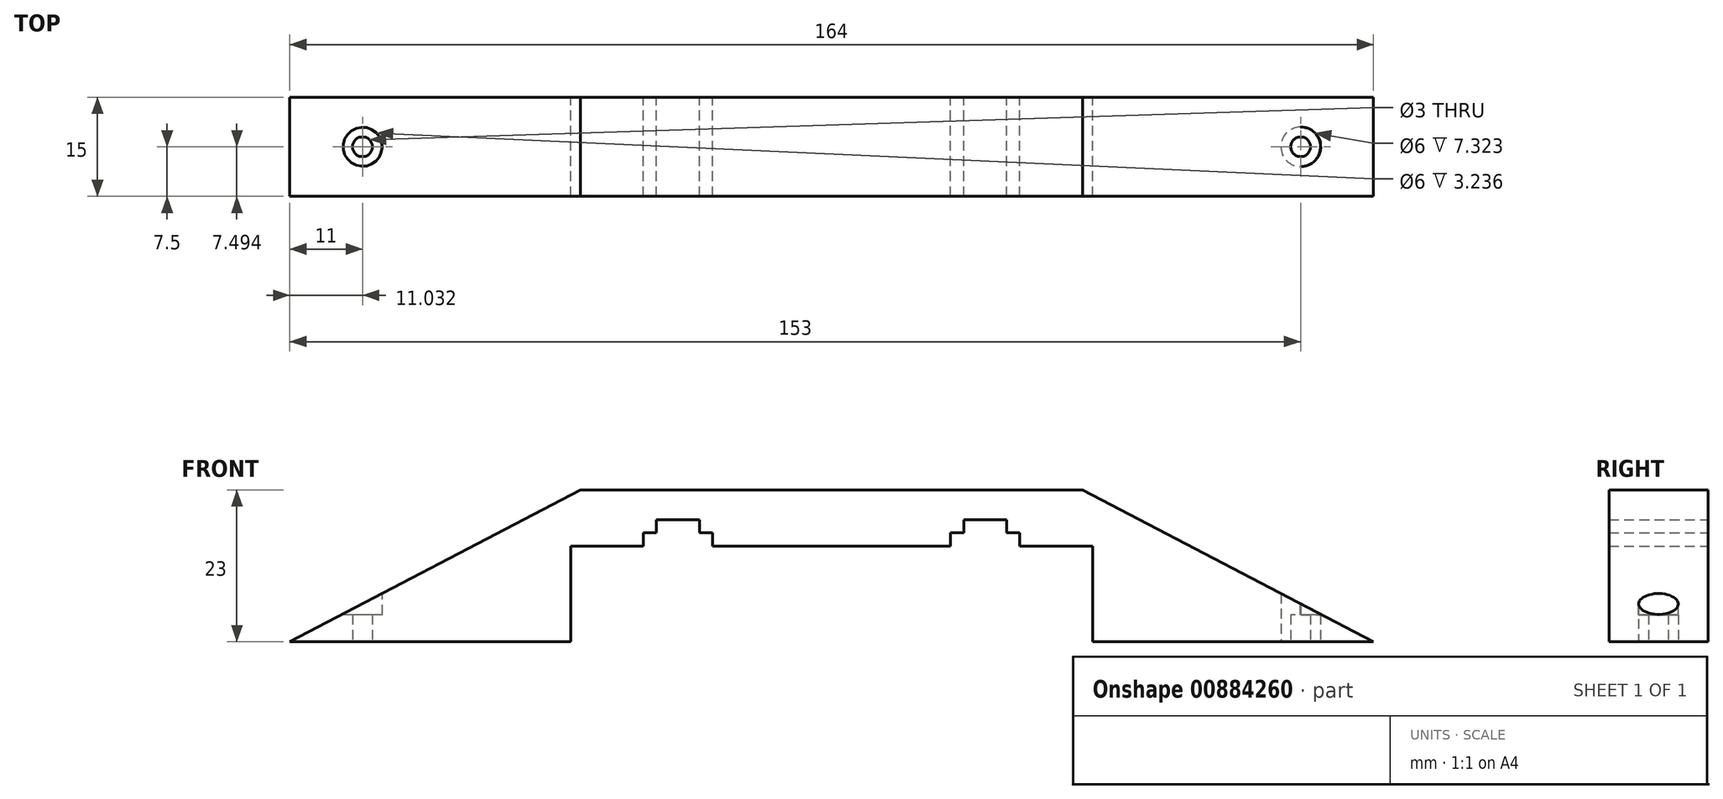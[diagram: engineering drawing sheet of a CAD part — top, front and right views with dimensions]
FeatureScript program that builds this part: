
annotation { "Feature Type Name" : "Feature", "Feature Type Description" : "" }
export const myFeature = defineFeature(function(context is Context, id is Id, definition is map)
    precondition{}
    {
        {
            var Q0;
            Q0=qCreatedBy(makeId("Top.planeOp"),FACE);
            cPlane(context, id + "F0", {"entities" : qUnion([Q0]), "cplaneType" : CPlaneType.OFFSET, "offset" : 8.6 * mm, "width" : 150 * mm, "height" : 150 * mm});
        }
        {
            var Q0;
            Q0=qCreatedBy(makeId("Front.planeOp"),FACE);
            var sketch = newSketch(context, id + "F1", { "sketchPlane" : qUnion([Q0])});
            skLineSegment(sketch, "E0", {"start": v(0, 122.54) * mm, "end": v(0, -122.54) * mm, "construction": true});
            skLineSegment(sketch, "E1", {"start": v(-39.5, 0) * mm, "end": v(-82, 0) * mm});
            skLineSegment(sketch, "E2", {"start": v(0, 0) * mm, "end": v(0, 14.5) * mm});
            skLineSegment(sketch, "E3", {"start": v(0, 23) * mm, "end": v(-38, 23) * mm});
            skLineSegment(sketch, "E4", {"start": v(-38, 23) * mm, "end": v(-82, 0) * mm});
            skLineSegment(sketch, "E5.top", {"start": v(0, 14.5) * mm, "end": v(-18, 14.5) * mm});
            skLineSegment(sketch, "E5.right", {"start": v(-39.5, 0) * mm, "end": v(-39.5, 14.5) * mm});
            skLineSegment(sketch, "E6.0", {"start": v(-20, 122.54) * mm, "end": v(-20, 16.5) * mm, "construction": true});
            skLineSegment(sketch, "E7.top", {"start": v(-20, 18.5) * mm, "end": v(-26.5, 18.5) * mm});
            skLineSegment(sketch, "E7.left", {"start": v(-20, 14.5) * mm, "end": v(-20, 18.5) * mm});
            skLineSegment(sketch, "E7.right", {"start": v(-26.5, 16.5) * mm, "end": v(-26.5, 18.5) * mm});
            skLineSegment(sketch, "E8.trimOffspring", {"start": v(-28.5, 14.5) * mm, "end": v(-39.5, 14.5) * mm});
            skLineSegment(sketch, "E9.MirrorCS", {"start": v(0, 23) * mm, "end": v(38, 23) * mm});
            skLineSegment(sketch, "E10.MirrorCS", {"start": v(38, 23) * mm, "end": v(82, 0) * mm});
            skLineSegment(sketch, "E11.MirrorCS", {"start": v(39.5, 0) * mm, "end": v(82, 0) * mm});
            skLineSegment(sketch, "E12.MirrorCS", {"start": v(39.5, 0) * mm, "end": v(39.5, 14.5) * mm});
            skLineSegment(sketch, "E13.MirrorCS", {"start": v(28.5, 14.5) * mm, "end": v(39.5, 14.5) * mm});
            skLineSegment(sketch, "E14.MirrorCS", {"start": v(20, 18.5) * mm, "end": v(26.5, 18.5) * mm});
            skLineSegment(sketch, "E15.MirrorCS", {"start": v(0, 14.5) * mm, "end": v(18, 14.5) * mm});
            skLineSegment(sketch, "E16.MirrorCS", {"start": v(20, 16.5) * mm, "end": v(20, 18.5) * mm});
            skLineSegment(sketch, "E17.MirrorCS", {"start": v(26.5, 16.5) * mm, "end": v(26.5, 18.5) * mm});
            skPoint(sketch, "E18.oppositeSnap0", {"position": v(-20, 16.5) * mm});
            skLineSegment(sketch, "E18.top", {"start": v(-28.5, 16.5) * mm, "end": v(-26.5, 16.5) * mm});
            skLineSegment(sketch, "E18.left", {"start": v(-28.5, 14.5) * mm, "end": v(-28.5, 16.5) * mm});
            skLineSegment(sketch, "E18.right", {"start": v(-18, 14.5) * mm, "end": v(-18, 16.5) * mm});
            skLineSegment(sketch, "E19.trimOffspring", {"start": v(-20, 16.5) * mm, "end": v(-18, 16.5) * mm});
            skPoint(sketch, "E20.orphan", {"position": v(-26.5, 14.5) * mm});
            skLineSegment(sketch, "E21.trimOffspring", {"start": v(-20, 14.5) * mm, "end": v(-20, -122.54) * mm, "construction": true});
            skLineSegment(sketch, "E22.MirrorCS", {"start": v(28.5, 16.5) * mm, "end": v(26.5, 16.5) * mm});
            skLineSegment(sketch, "E23.MirrorCS", {"start": v(28.5, 14.5) * mm, "end": v(28.5, 16.5) * mm});
            skLineSegment(sketch, "E24.MirrorCS", {"start": v(20, 16.5) * mm, "end": v(18, 16.5) * mm});
            skLineSegment(sketch, "E25.MirrorCS", {"start": v(18, 14.5) * mm, "end": v(18, 16.5) * mm});
            skPoint(sketch, "E26.orphan", {"position": v(20, 14.5) * mm});
            skPoint(sketch, "E27.orphan", {"position": v(26.5, 14.5) * mm});
            skSolve(sketch);
        }
        {
            var Q0;
            Q0=makeQuery(id+"F1.imprint","IMPRINT",FACE,{"disambiguationData":[TD([[makeQuery(id+"F1.imprint","IMPRINT",EDGE,{"derivedFrom":sQuery(id+"F1.wireOp",EDGE,"E1")}),-1.0]])]});
            extrude(context, id + "F2", {"entities" : qUnion([Q0]), "depth" : 15 * mm, "offsetDistance" : 25 * mm});
        }
        {
            var Q0;
            Q0=qCreatedBy(makeId("Top.planeOp"),FACE);
            var sketch = newSketch(context, id + "F3", { "sketchPlane" : qUnion([Q0])});
            skLineSegment(sketch, "E28", {"start": v(0, 0) * mm, "end": v(-3.58, 0) * mm, "construction": true});
            skLineSegment(sketch, "E29", {"start": v(-109.94, 0) * mm, "end": v(106.23, 0) * mm, "construction": true});
            skLineSegment(sketch, "E30.0", {"start": v(-109.94, -7.5) * mm, "end": v(106.23, -7.5) * mm, "construction": true});
            skLineSegment(sketch, "E31", {"start": v(-82, -15) * mm, "end": v(-82, 17.83) * mm, "construction": true});
            skLineSegment(sketch, "E32.0", {"start": v(-71, -15) * mm, "end": v(-71, 17.83) * mm, "construction": true});
            skCircle(sketch, "E33", {"center": v(-71, -7.5) * mm, "radius": 1.5 * mm});
            skLineSegment(sketch, "E34", {"start": v(0, 23.95) * mm, "end": v(0, -38.43) * mm, "construction": true});
            skCircle(sketch, "E35.MirrorC", {"center": v(71, -7.5) * mm, "radius": 1.5 * mm});
            skCircle(sketch, "E36", {"center": v(-71, -7.5) * mm, "radius": 3 * mm});
            skCircle(sketch, "E37.MirrorC", {"center": v(71, -7.5) * mm, "radius": 3 * mm});
            skSolve(sketch);
        }
        {
            var Q0;
            Q0=makeQuery(id+"F3.imprint","IMPRINT",FACE,{"disambiguationData":[TD([[makeQuery(id+"F3.imprint","IMPRINT",EDGE,{"derivedFrom":sQuery(id+"F3.wireOp",EDGE,"E35.MirrorC")}),-1.0]])]});
            var Q1;
            Q1=makeQuery(id+"F3.imprint","IMPRINT",FACE,{"disambiguationData":[TD([[makeQuery(id+"F3.imprint","IMPRINT",EDGE,{"derivedFrom":sQuery(id+"F3.wireOp",EDGE,"E33")}),1.0]])]});
            extrude(context, id + "F4", {"entities" : qUnion([Q0, Q1]), "operationType" : NewBodyOperationType.REMOVE, "endBound" : BoundingType.THROUGH_ALL, "depth" : 25 * mm, "offsetDistance" : 25 * mm});
        }
        {
            var Q0;
            Q0=qCreatedBy(id+"F0.planeOp",FACE);
            var sketch = newSketch(context, id + "F5", { "sketchPlane" : qUnion([Q0])});
            skCircle(sketch, "E38", {"center": v(-70.97, -7.5) * mm, "radius": 3 * mm});
            skCircle(sketch, "E39", {"center": v(71.06, -7.5) * mm, "radius": 3 * mm});
            skSolve(sketch);
        }
        {
            var Q0;
            Q0=makeQuery(id+"F5.imprint","IMPRINT",FACE,{"disambiguationData":[TD([[makeQuery(id+"F5.imprint","IMPRINT",EDGE,{"derivedFrom":sQuery(id+"F5.wireOp",EDGE,"E38")}),1.0]])]});
            var Q1;
            Q1=makeQuery(id+"F5.imprint","IMPRINT",FACE,{"disambiguationData":[TD([[makeQuery(id+"F5.imprint","IMPRINT",EDGE,{"derivedFrom":sQuery(id+"F5.wireOp",EDGE,"E39")}),1.0]])]});
            extrude(context, id + "F6", {"entities" : qUnion([Q0, Q1]), "operationType" : NewBodyOperationType.REMOVE, "oppositeDirection" : true, "depth" : 4.5 * mm, "offsetDistance" : 25 * mm});
        }
        {
            var Q0;
            Q0=qCreatedBy(makeId("Top.planeOp"),FACE);
            cPlane(context, id + "F7", {"entities" : qUnion([Q0]), "cplaneType" : CPlaneType.OFFSET, "offset" : 23 * mm, "width" : 150 * mm, "height" : 150 * mm});
        }
        {
            var Q0;
            Q0=qCreatedBy(id+"F7.planeOp",FACE);
            var sketch = newSketch(context, id + "F8", { "sketchPlane" : qUnion([Q0])});
            skLineSegment(sketch, "E40", {"start": v(38, -15) * mm, "end": v(-38, 0) * mm, "construction": true});
            skLineSegment(sketch, "E41", {"start": v(-38, -15) * mm, "end": v(38, 0) * mm, "construction": true});
            skLineSegment(sketch, "E42.0", {"start": v(38, -13.47) * mm, "end": v(7.75, -7.5) * mm});
            skLineSegment(sketch, "E43.0", {"start": v(30.25, -15) * mm, "end": v(0, -9.03) * mm});
            skLineSegment(sketch, "E44.0", {"start": v(-30.25, -15) * mm, "end": v(0, -9.03) * mm});
            skLineSegment(sketch, "E45.0", {"start": v(-38, -13.47) * mm, "end": v(-7.75, -7.5) * mm});
            skLineSegment(sketch, "E46", {"start": v(-38, -15) * mm, "end": v(-38, -13.47) * mm});
            skLineSegment(sketch, "E47", {"start": v(-38, -15) * mm, "end": v(-30.25, -15) * mm});
            skLineSegment(sketch, "E48", {"start": v(-38, 0) * mm, "end": v(-38, -1.53) * mm});
            skLineSegment(sketch, "E49", {"start": v(-38, 0) * mm, "end": v(-30.25, 0) * mm});
            skLineSegment(sketch, "E50.trimOffspring", {"start": v(0, -5.97) * mm, "end": v(30.25, 0) * mm});
            skLineSegment(sketch, "E51.trimOffspring", {"start": v(-7.75, -7.5) * mm, "end": v(-38, -1.53) * mm});
            skLineSegment(sketch, "E52.trimOffspring", {"start": v(7.75, -7.5) * mm, "end": v(38, -1.53) * mm});
            skLineSegment(sketch, "E53.trimOffspring", {"start": v(0, -5.97) * mm, "end": v(-30.25, 0) * mm});
            skLineSegment(sketch, "E54", {"start": v(38, -15) * mm, "end": v(38, -13.47) * mm});
            skLineSegment(sketch, "E55", {"start": v(38, -13.47) * mm, "end": v(38, -15) * mm});
            skLineSegment(sketch, "E56", {"start": v(38, -15) * mm, "end": v(30.25, -15) * mm});
            skLineSegment(sketch, "E57", {"start": v(38, -1.53) * mm, "end": v(38, 0) * mm});
            skLineSegment(sketch, "E58", {"start": v(38, 0) * mm, "end": v(30.25, 0) * mm});
            skSolve(sketch);
        }
        {
            var Q0;
            Q0 = qSketchRegion(id + "F8", true);
            extrude(context, id + "F9", {"entities" : qUnion([Q0]), "operationType" : NewBodyOperationType.ADD, "oppositeDirection" : true, "depth" : 4.3 * mm, "offsetDistance" : 25 * mm});
        }
    });
